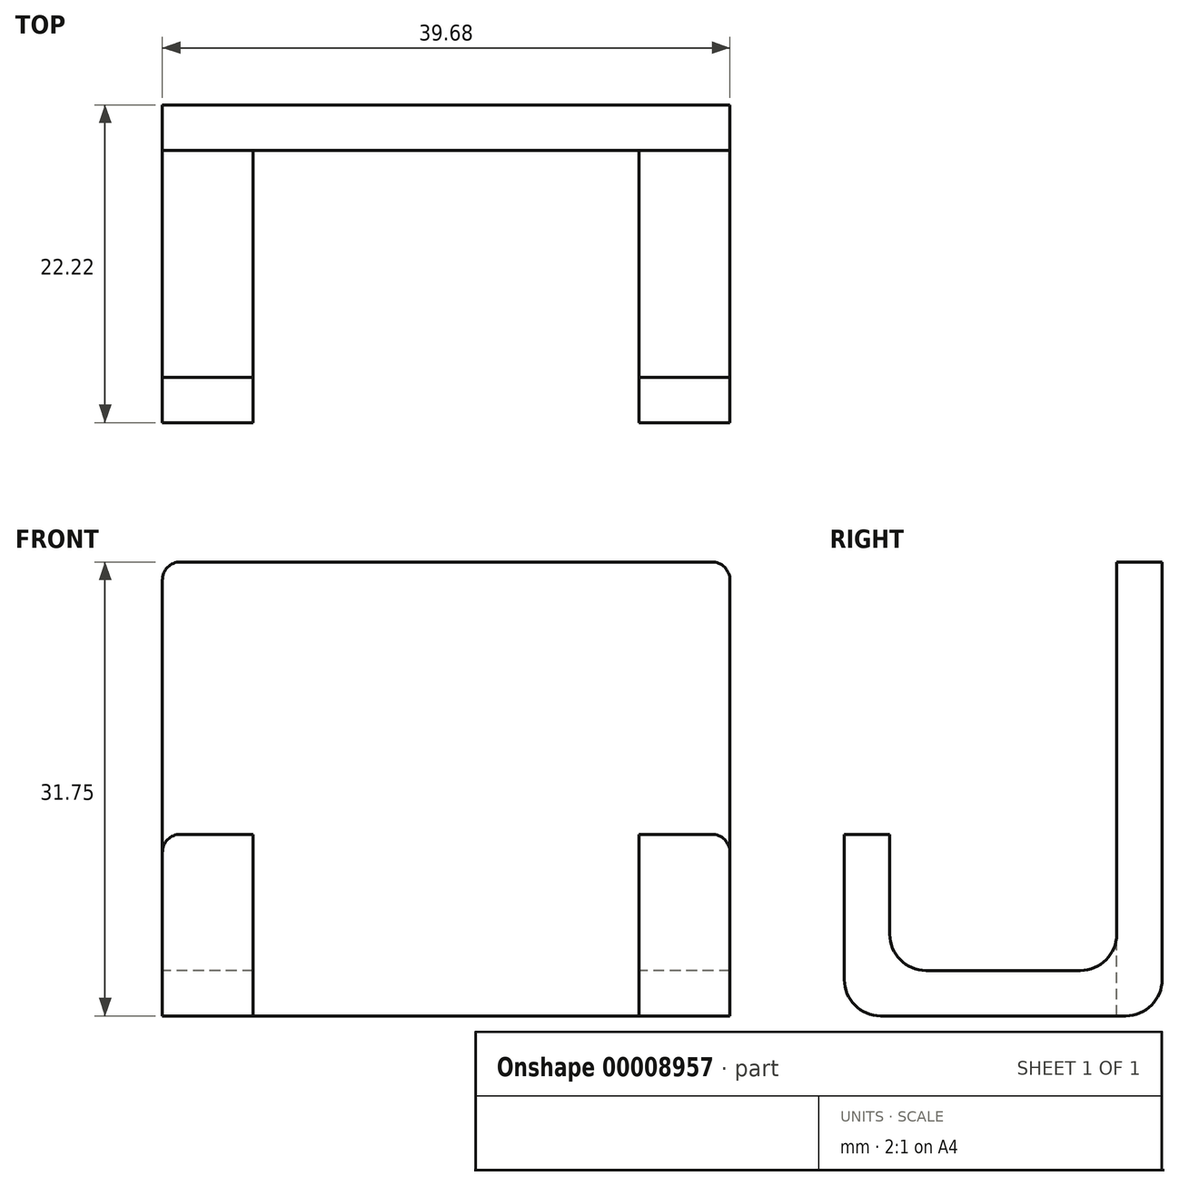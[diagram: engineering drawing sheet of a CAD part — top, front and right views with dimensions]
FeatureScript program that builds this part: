
annotation { "Feature Type Name" : "Feature", "Feature Type Description" : "" }
export const myFeature = defineFeature(function(context is Context, id is Id, definition is map)
    precondition{}
    {
        {
            var Q0;
            Q0=qCreatedBy(makeId("Right.planeOp"),FACE);
            var sketch = newSketch(context, id + "F0", { "sketchPlane" : qUnion([Q0])});
            skLineSegment(sketch, "E0", {"start": v(-8.57, 0) * mm, "end": v(8.57, 0) * mm});
            skLineSegment(sketch, "E1", {"start": v(11.11, 2.54) * mm, "end": v(11.11, 31.75) * mm});
            skLineSegment(sketch, "E2", {"start": v(11.11, 31.75) * mm, "end": v(7.94, 31.75) * mm});
            skLineSegment(sketch, "E3", {"start": v(7.94, 31.75) * mm, "end": v(7.94, 5.72) * mm});
            skLineSegment(sketch, "E4", {"start": v(5.4, 3.18) * mm, "end": v(-5.4, 3.17) * mm});
            skLineSegment(sketch, "E5", {"start": v(-7.94, 5.72) * mm, "end": v(-7.94, 12.7) * mm});
            skLineSegment(sketch, "E6", {"start": v(-7.94, 12.7) * mm, "end": v(-11.11, 12.7) * mm});
            skLineSegment(sketch, "E7", {"start": v(-11.11, 12.7) * mm, "end": v(-11.11, 2.54) * mm});
            skPoint(sketch, "E8.visualSharp", {"position": v(-11.11, 0) * mm});
            skArc(sketch, "E8.filletArc", {"start": v(-11.11, 2.54) * mm, "mid": v(-10.37, 0.74) * mm, "end": v(-8.57, 0) * mm});
            skPoint(sketch, "E9.visualSharp", {"position": v(-7.94, 3.17) * mm});
            skArc(sketch, "E9.filletArc", {"start": v(-7.94, 5.72) * mm, "mid": v(-7.2, 3.92) * mm, "end": v(-5.4, 3.17) * mm});
            skPoint(sketch, "E10.visualSharp", {"position": v(7.94, 3.18) * mm});
            skArc(sketch, "E10.filletArc", {"start": v(5.4, 3.18) * mm, "mid": v(7.2, 3.92) * mm, "end": v(7.94, 5.72) * mm});
            skPoint(sketch, "E11.visualSharp", {"position": v(11.11, 0) * mm});
            skArc(sketch, "E11.filletArc", {"start": v(8.57, 0) * mm, "mid": v(10.37, 0.74) * mm, "end": v(11.11, 2.54) * mm});
            skSolve(sketch);
        }
        {
            var Q0;
            Q0=makeQuery(id+"F0.imprint","IMPRINT",FACE,{"disambiguationData":[TD([[makeQuery(id+"F0.imprint","IMPRINT",EDGE,{"derivedFrom":sQuery(id+"F0.wireOp",EDGE,"E0")}),1.0]])]});
            extrude(context, id + "F1", {"entities" : qUnion([Q0]), "depth" : 39.69 * mm, "offsetDistance" : 25.4 * mm, "symmetric" : true});
        }
        {
            var Q0;
            Q0=makeQuery(id+"F1.opExtrude","SWEPT_FACE",FACE,{"disambiguationData":[OSD([sQuery(id+"F0.wireOp",EDGE,"E6")])]});
            var sketch = newSketch(context, id + "F2", { "sketchPlane" : qUnion([Q0])});
            skLineSegment(sketch, "E12.0", {"start": v(19.84, 7.94) * mm, "end": v(-19.84, 7.94) * mm});
            skLineSegment(sketch, "E13.0", {"start": v(19.84, -11.11) * mm, "end": v(-19.84, -11.11) * mm});
            skLineSegment(sketch, "E14.0", {"start": v(-19.84, -7.94) * mm, "end": v(-19.84, -11.11) * mm});
            skLineSegment(sketch, "E15.0", {"start": v(19.84, -7.94) * mm, "end": v(19.84, -11.11) * mm});
            skLineSegment(sketch, "E16", {"start": v(-13.5, 7.94) * mm, "end": v(-13.5, -11.11) * mm});
            skLineSegment(sketch, "E17", {"start": v(13.5, -11.11) * mm, "end": v(13.5, 7.94) * mm});
            skSolve(sketch);
        }
        {
            var Q0;
            {var subQ0=sQuery(id+"F2.wireOp",EDGE,"E16");var subQ1=sQuery(id+"F2.wireOp",EDGE,"E12.0");var subQ2=makeQuery(id+"F2.imprint","INTERSECT",VERTEX,{"derivedFrom":[subQ1,subQ0]});Q0=makeQuery(id+"F2.imprint","IMPRINT",FACE,{"disambiguationData":[TD([[makeQuery(id+"F2.imprint","IMPRINT",EDGE,{"disambiguationData":[TD([[subQ2,1.0]])],"derivedFrom":subQ1}),1.0]])]});}
            var Q1;
            {var subQ0=sQuery(id+"F2.wireOp",EDGE,"E16");var subQ1=sQuery(id+"F2.wireOp",EDGE,"E13.0");var subQ2=makeQuery(id+"F2.imprint","INTERSECT",VERTEX,{"derivedFrom":[subQ1,subQ0]});Q1=makeQuery(id+"F2.imprint","IMPRINT",FACE,{"disambiguationData":[TD([[makeQuery(id+"F2.imprint","IMPRINT",EDGE,{"disambiguationData":[TD([[subQ2,1.0]])],"derivedFrom":subQ1}),-1.0]])]});}
            extrude(context, id + "F3", {"entities" : qUnion([Q0, Q1]), "operationType" : NewBodyOperationType.REMOVE, "endBound" : BoundingType.THROUGH_ALL, "oppositeDirection" : true, "depth" : 25.4 * mm, "offsetDistance" : 25.4 * mm});
        }
        {
            var Q0;
            Q0=makeQuery(id+"F1.opExtrude","CAP_EDGE",EDGE,{"disambiguationData":[OSD([sQuery(id+"F0.wireOp",EDGE,"E6")])],"isStart":true});
            var Q1;
            Q1=makeQuery(id+"F3.boolean.opBoolean","COPY",EDGE,{"derivedFrom":makeQuery(id+"F3.opExtrude","CAP_EDGE",EDGE,{"disambiguationData":[OSD([sQuery(id+"F2.wireOp",EDGE,"E16")])],"isStart":true})});
            var Q2;
            Q2=makeQuery(id+"F3.boolean.opBoolean","COPY",EDGE,{"derivedFrom":makeQuery(id+"F3.opExtrude","CAP_EDGE",EDGE,{"disambiguationData":[OSD([sQuery(id+"F2.wireOp",EDGE,"E17")])],"isStart":true})});
            var Q3;
            Q3=makeQuery(id+"F1.opExtrude","CAP_EDGE",EDGE,{"disambiguationData":[OSD([sQuery(id+"F0.wireOp",EDGE,"E6")])],"isStart":false});
            fillet(context, id + "F4", {"entities" : qUnion([Q0, Q1, Q2, Q3]), "radius" : 1.27 * mm, "tangentPropagation" : true, "allowEdgeOverflow" : false});
        }
        {
            var Q0;
            Q0=makeQuery(id+"F1.opExtrude","CAP_EDGE",EDGE,{"disambiguationData":[OSD([sQuery(id+"F0.wireOp",EDGE,"E2")])],"isStart":true});
            var Q1;
            Q1=makeQuery(id+"F1.opExtrude","CAP_EDGE",EDGE,{"disambiguationData":[OSD([sQuery(id+"F0.wireOp",EDGE,"E2")])],"isStart":false});
            fillet(context, id + "F5", {"entities" : qUnion([Q0, Q1]), "radius" : 1.27 * mm, "tangentPropagation" : true, "allowEdgeOverflow" : false});
        }
    });
